# Revit family: Gira_5366005
name_source: partatom
category: Electrical Fixtures
revit_build: Autodesk Revit 2017 (Build: 20160225_1515(x64)
units: mm (PartAtom-declared; Revit-internal decimal feet)

## family parameters
Cut with Voids When Loaded = No
Host = Face
Maintain Annotation Orientation = No
Part Type = Normal
Room Calculation Point = No
Round Connector Dimension = Use Diameter
Shared = No

## types (1)
- S3000 blind timer + timer Display System 55 black m
    Application = Control of electrical users
    Available = No
    BIM (1) = https://media.stage.bim.site und Tasten.rfa?public/gira/36a6b08/Sys55_Abdeckung_Schalten und Tasten.rfa
    Category = Intelligent control element
    Data sheet (1) = https://katalog.gira.de
    Default Elevation = 1219 mm
    Description = S3000 blind tim. tim.Displ. Sys55 BKm,System 3000 blind timer and timer Display,,black matt,Features:,- Operation via capacitive sensor surface.,- Fast programming for adopting the current time as the programmed movement time switching time.,- Automatic summer winter time switchover, deactivatable.,- Switching at sunrise or sunset (astro function) adjustable for 18 countries.,- Astro time for sunrise and sunset can be individually adjusted by +-2 hours.,- The blocking function blocks operation of the auxiliary unit and deactivates automatic mode.,- The display turns off after 2 minutes, permanent display of time is possible.,- Programming of one raising and one lowering time or two switch-on and switch-off times for each day in week segments Mon-Fri and Sat+Sun.
    GTIN = 4010337037484
    HAN = 5366005
    HeinzeBIM = https://bimportal.heinze.de
    Manufacturer = Gira
    Manufacturer URL = https://www.gira.de
    Name = S3000 blind timer + timer Display System 55 black m
    Number of actuation points = 4
    Number of buttons = 2
    Suitable for application with dimmer = No
    Suitable for application with switch = No
    Suitable for application with venetian shutter switch = Yes
    Transparent = No
    URL = http://katalog.gira.de
    With LED indication = Yes
    With cover = Yes

## geometry (parser evidence)
native form markers: Blend x2, Sweep x9
no freeform markers — native parametric forms only
